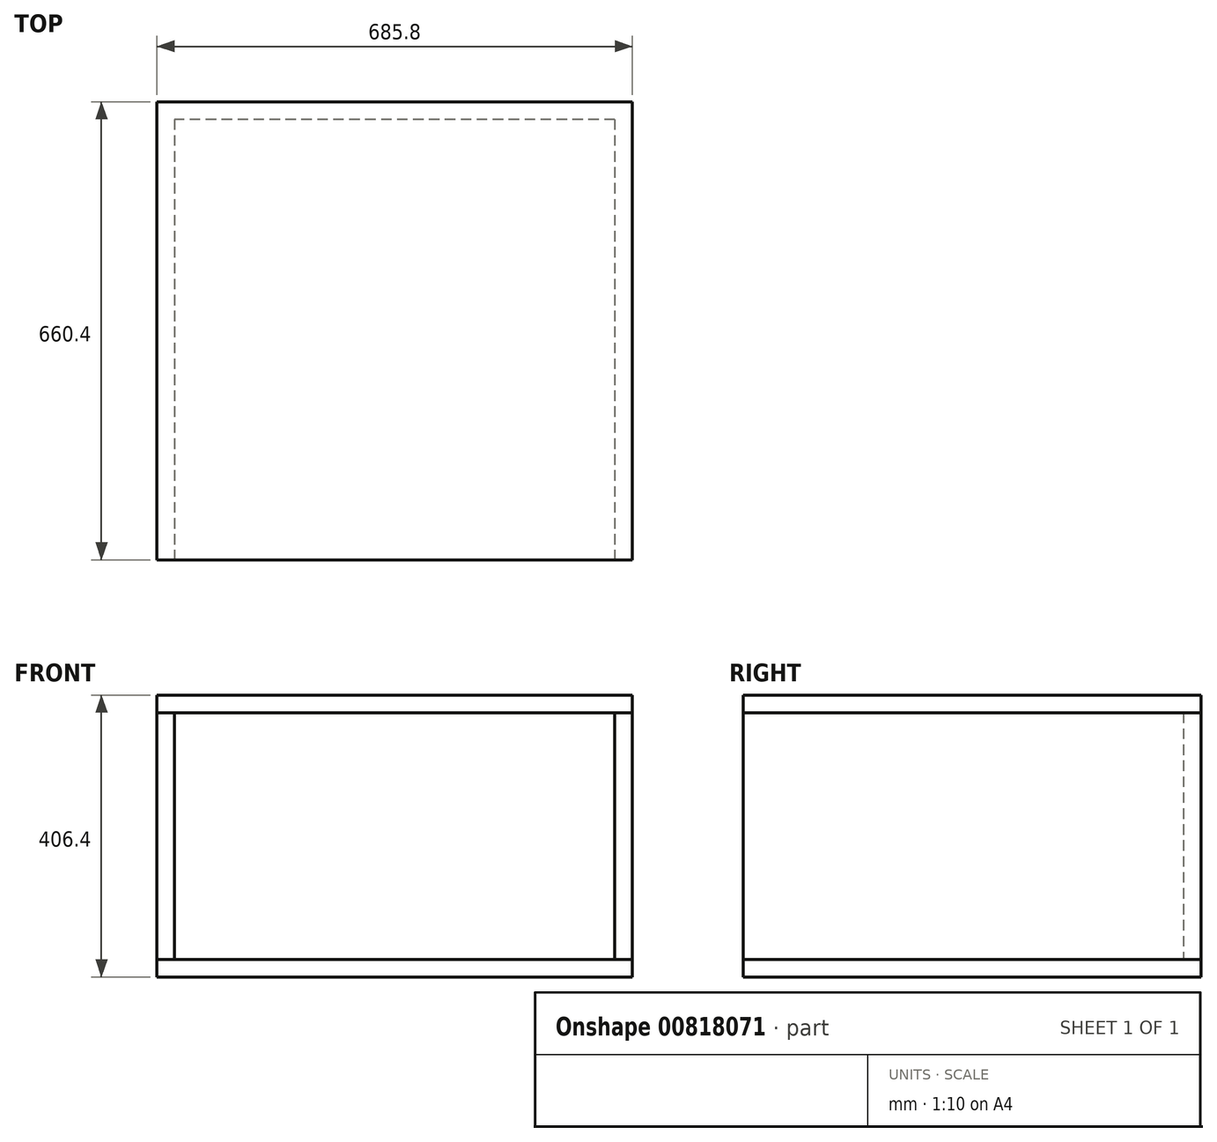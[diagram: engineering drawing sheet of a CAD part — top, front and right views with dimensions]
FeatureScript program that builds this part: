
annotation { "Feature Type Name" : "Feature", "Feature Type Description" : "" }
export const myFeature = defineFeature(function(context is Context, id is Id, definition is map)
    precondition{}
    {
        {
            var Q0;
            Q0=qCreatedBy(makeId("Top.planeOp"),FACE);
            var sketch = newSketch(context, id + "F0", { "sketchPlane" : qUnion([Q0])});
            skLineSegment(sketch, "E0.bottom", {"start": v(342.9, 330.2) * mm, "end": v(-342.9, 330.2) * mm});
            skLineSegment(sketch, "E0.top", {"start": v(342.9, -330.2) * mm, "end": v(-342.9, -330.2) * mm});
            skLineSegment(sketch, "E0.left", {"start": v(342.9, 330.2) * mm, "end": v(342.9, -330.2) * mm});
            skLineSegment(sketch, "E0.right", {"start": v(-342.9, 330.2) * mm, "end": v(-342.9, -330.2) * mm});
            skPoint(sketch, "E0.middle", {"position": v(0, 0) * mm});
            skSolve(sketch);
        }
        {
            var Q0;
            Q0 = qSketchRegion(id + "F0", true);
            extrude(context, id + "F1", {"entities" : qUnion([Q0]), "depth" : 25.4 * mm, "offsetDistance" : 25.4 * mm});
        }
        {
            var Q0;
            Q0=makeQuery(id+"F1.opExtrude","CAP_FACE",FACE,{"disambiguationData":[OSD([sQuery(id+"F0.wireOp",EDGE,"E0.bottom"),sQuery(id+"F0.wireOp",EDGE,"E0.top"),sQuery(id+"F0.wireOp",EDGE,"E0.left"),sQuery(id+"F0.wireOp",EDGE,"E0.right")])],"isStart":false});
            var sketch = newSketch(context, id + "F2", { "sketchPlane" : qUnion([Q0])});
            skLineSegment(sketch, "E1.0", {"start": v(-342.9, 330.2) * mm, "end": v(-342.9, -330.2) * mm});
            skLineSegment(sketch, "E2.0", {"start": v(342.9, 330.2) * mm, "end": v(-342.9, 330.2) * mm});
            skLineSegment(sketch, "E3.0", {"start": v(342.9, 330.2) * mm, "end": v(342.9, -330.2) * mm});
            skLineSegment(sketch, "E4.0", {"start": v(-317.5, 304.8) * mm, "end": v(-317.5, -330.2) * mm});
            skLineSegment(sketch, "E4.1", {"start": v(317.5, 304.8) * mm, "end": v(-317.5, 304.8) * mm});
            skLineSegment(sketch, "E4.2", {"start": v(317.5, 304.8) * mm, "end": v(317.5, -330.2) * mm});
            skLineSegment(sketch, "E5", {"start": v(-342.9, -330.2) * mm, "end": v(-317.5, -330.2) * mm});
            skLineSegment(sketch, "E6", {"start": v(317.5, -330.2) * mm, "end": v(342.9, -330.2) * mm});
            skSolve(sketch);
        }
        {
            var Q0;
            Q0 = qSketchRegion(id + "F2", true);
            extrude(context, id + "F3", {"entities" : qUnion([Q0]), "depth" : 355.6 * mm, "offsetDistance" : 25.4 * mm});
        }
        {
            var Q0;
            Q0=makeQuery(id+"F3.opExtrude","CAP_FACE",FACE,{"disambiguationData":[OSD([sQuery(id+"F2.wireOp",EDGE,"E1.0"),sQuery(id+"F2.wireOp",EDGE,"E2.0"),sQuery(id+"F2.wireOp",EDGE,"E3.0"),sQuery(id+"F2.wireOp",EDGE,"E4.0"),sQuery(id+"F2.wireOp",EDGE,"E4.1"),sQuery(id+"F2.wireOp",EDGE,"E4.2"),sQuery(id+"F2.wireOp",EDGE,"E5"),sQuery(id+"F2.wireOp",EDGE,"E6")])],"isStart":false});
            var sketch = newSketch(context, id + "F4", { "sketchPlane" : qUnion([Q0])});
            skLineSegment(sketch, "E7.bottom", {"start": v(-342.9, 330.2) * mm, "end": v(342.9, 330.2) * mm});
            skLineSegment(sketch, "E7.top", {"start": v(-342.9, -330.2) * mm, "end": v(342.9, -330.2) * mm});
            skLineSegment(sketch, "E7.left", {"start": v(-342.9, 330.2) * mm, "end": v(-342.9, -330.2) * mm});
            skLineSegment(sketch, "E7.right", {"start": v(342.9, 330.2) * mm, "end": v(342.9, -330.2) * mm});
            skSolve(sketch);
        }
        {
            var Q0;
            Q0 = qSketchRegion(id + "F4", true);
            extrude(context, id + "F5", {"entities" : qUnion([Q0]), "depth" : 25.4 * mm, "offsetDistance" : 25.4 * mm});
        }
    });
